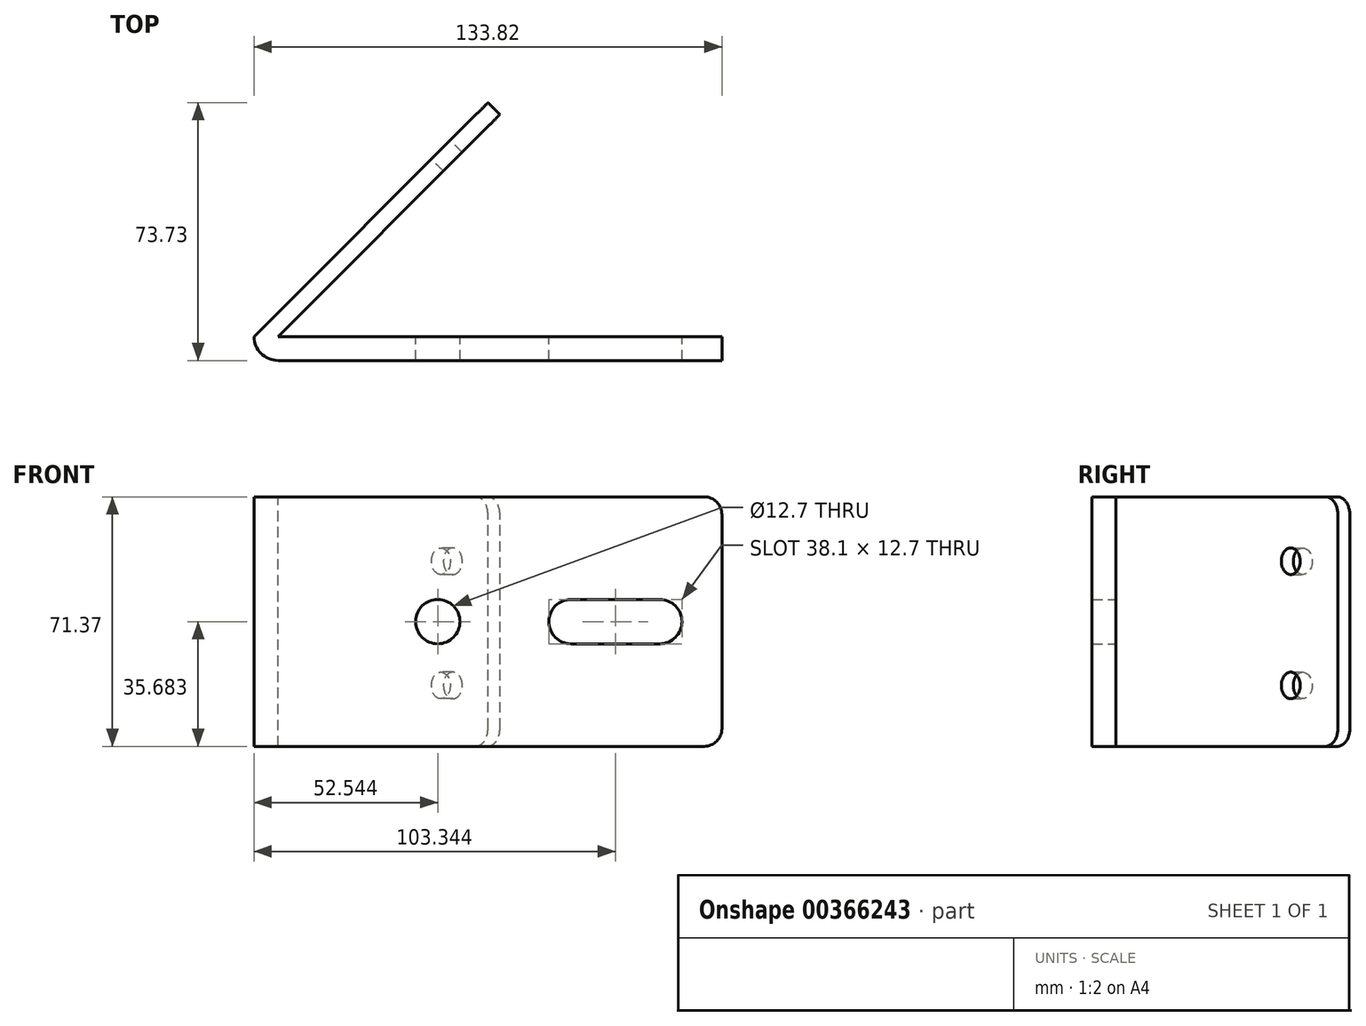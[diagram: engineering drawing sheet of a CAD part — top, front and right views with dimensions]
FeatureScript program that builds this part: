
annotation { "Feature Type Name" : "Feature", "Feature Type Description" : "" }
export const myFeature = defineFeature(function(context is Context, id is Id, definition is map)
    precondition{}
    {
        {
            var Q0;
            Q0=qCreatedBy(makeId("Top.planeOp"),FACE);
            var sketch = newSketch(context, id + "F0", { "sketchPlane" : qUnion([Q0])});
            skLineSegment(sketch, "E0", {"start": v(0, 0) * mm, "end": v(98.16, 0) * mm});
            skLineSegment(sketch, "E1", {"start": v(98.16, 0) * mm, "end": v(98.16, -6.82) * mm});
            skLineSegment(sketch, "E2", {"start": v(98.16, -6.82) * mm, "end": v(-28.84, -6.82) * mm});
            skArc(sketch, "E3", {"start": v(-28.84, -6.82) * mm, "mid": v(-33.66, -4.83) * mm, "end": v(-35.66, 0) * mm});
            skLineSegment(sketch, "E4", {"start": v(-35.66, 0) * mm, "end": v(31.25, 66.91) * mm});
            skLineSegment(sketch, "E5", {"start": v(31.25, 66.91) * mm, "end": v(34.66, 63.5) * mm});
            skLineSegment(sketch, "E6", {"start": v(-28.84, 0) * mm, "end": v(34.66, 63.5) * mm});
            skLineSegment(sketch, "E7", {"start": v(-28.84, 0) * mm, "end": v(0, 0) * mm});
            skSolve(sketch);
        }
        {
            var Q0;
            Q0=makeQuery(id+"F0.imprint","IMPRINT",FACE,{"disambiguationData":[TD([[makeQuery(id+"F0.imprint","IMPRINT",EDGE,{"derivedFrom":sQuery(id+"F0.wireOp",EDGE,"E0")}),-1.0]])]});
            extrude(context, id + "F1", {"entities" : qUnion([Q0]), "oppositeDirection" : true, "depth" : 71.37 * mm});
        }
        {
            var Q0;
            Q0=makeQuery(id+"F1.opExtrude","CAP_EDGE",EDGE,{"disambiguationData":[OSD([sQuery(id+"F0.wireOp",EDGE,"E5")])],"isStart":true});
            var Q1;
            Q1=makeQuery(id+"F1.opExtrude","CAP_EDGE",EDGE,{"disambiguationData":[OSD([sQuery(id+"F0.wireOp",EDGE,"E5")])],"isStart":false});
            var Q2;
            Q2=makeQuery(id+"F1.opExtrude","CAP_EDGE",EDGE,{"disambiguationData":[OSD([sQuery(id+"F0.wireOp",EDGE,"E1")])],"isStart":true});
            var Q3;
            Q3=makeQuery(id+"F1.opExtrude","CAP_EDGE",EDGE,{"disambiguationData":[OSD([sQuery(id+"F0.wireOp",EDGE,"E1")])],"isStart":false});
            fillet(context, id + "F2", {"entities" : qUnion([Q0, Q1, Q2, Q3]), "radius" : 5.08 * mm, "tangentPropagation" : true, "allowEdgeOverflow" : false});
        }
        {
            var Q0;
            Q0=makeQuery(id+"F1.opExtrude","SWEPT_FACE",FACE,{"disambiguationData":[OSD([sQuery(id+"F0.wireOp",EDGE,"E7")])]});
            var sketch = newSketch(context, id + "F3", { "sketchPlane" : qUnion([Q0])});
            skCircle(sketch, "E8", {"center": v(-16.88, -35.69) * mm, "radius": 6.35 * mm});
            skPoint(sketch, "E8.centerSnap0", {"position": v(28.84, -35.69) * mm});
            skArc(sketch, "E9", {"start": v(-54.98, -29.34) * mm, "mid": v(-48.63, -35.69) * mm, "end": v(-54.98, -42.04) * mm});
            skLineSegment(sketch, "E10", {"start": v(-54.98, -42.04) * mm, "end": v(-80.38, -42.04) * mm});
            skLineSegment(sketch, "E11", {"start": v(-54.98, -29.34) * mm, "end": v(-80.38, -29.34) * mm});
            skArc(sketch, "E12", {"start": v(-80.38, -42.04) * mm, "mid": v(-86.73, -35.69) * mm, "end": v(-80.38, -29.34) * mm});
            skSolve(sketch);
        }
        {
            var Q0;
            Q0=makeQuery(id+"F3.imprint","IMPRINT",FACE,{"disambiguationData":[TD([[makeQuery(id+"F3.imprint","IMPRINT",EDGE,{"derivedFrom":sQuery(id+"F3.wireOp",EDGE,"E8")}),1.0]])]});
            extrude(context, id + "F4", {"entities" : qUnion([Q0]), "operationType" : NewBodyOperationType.REMOVE, "oppositeDirection" : true, "depth" : 25.4 * mm});
        }
        {
            var Q0;
            Q0 = qSketchRegion(id + "F3", true);
            extrude(context, id + "F5", {"entities" : qUnion([Q0]), "operationType" : NewBodyOperationType.REMOVE, "oppositeDirection" : true, "depth" : 25.4 * mm});
        }
        {
            var Q0;
            Q0=makeQuery(id+"F1.opExtrude","SWEPT_FACE",FACE,{"disambiguationData":[OSD([sQuery(id+"F0.wireOp",EDGE,"E4")])]});
            var sketch = newSketch(context, id + "F6", { "sketchPlane" : qUnion([Q0])});
            skCircle(sketch, "E13", {"center": v(-50.36, -53.95) * mm, "radius": 3.81 * mm});
            skCircle(sketch, "E14", {"center": v(-50.36, -18.43) * mm, "radius": 3.81 * mm});
            skSolve(sketch);
        }
        {
            var Q0;
            Q0=makeQuery(id+"F6.imprint","IMPRINT",FACE,{"disambiguationData":[TD([[makeQuery(id+"F6.imprint","IMPRINT",EDGE,{"derivedFrom":sQuery(id+"F6.wireOp",EDGE,"E13")}),1.0]])]});
            var Q1;
            Q1=makeQuery(id+"F6.imprint","IMPRINT",FACE,{"disambiguationData":[TD([[makeQuery(id+"F6.imprint","IMPRINT",EDGE,{"derivedFrom":sQuery(id+"F6.wireOp",EDGE,"E14")}),1.0]])]});
            extrude(context, id + "F7", {"entities" : qUnion([Q0, Q1]), "operationType" : NewBodyOperationType.REMOVE, "oppositeDirection" : true, "depth" : 25.4 * mm});
        }
    });
